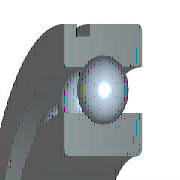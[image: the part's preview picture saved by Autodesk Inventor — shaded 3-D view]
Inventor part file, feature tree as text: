
AUTODESK INVENTOR PART (.ipt)
format: ipt  version: 2015 (Build 190159000, 159)  size: 322,560 bytes
history: native  units: mm (DEFAULTED — no unit token found)
features: sketch x1, other x1, pattern_circular x1
ambient origin geometry x8: Origin, YZ Plane, XZ Plane, XY Plane, X Axis, Y Axis, Z Axis, Center Point
bodies: Solid1 (feature_tree)
feature tree (3):
  sketch  "草图"  dims[d0=7.02mm d17=90.0deg d18=90.0deg d1=1.0mm d2=90.0mm d3=360.0deg d4=0.0mm d5=0.0mm d6=0.0mm d7=25.0mm d8=52.0mm d9=38.5mm d10=48.4mm d11=33.802mm d12=33.802mm d13=33.802mm d14=0.0mm d15=15.0mm d16=15.0mm d19=2.5mm d20=5.0mm d22=7.5mm d23=0.0mm d24=0.0mm]
  other  "轴承体"
  pattern_circular  "IDS_ARRAYBALL[SIMPL:T]"  Angle=90.0deg  [1 undecoded]
note: 1 required parameter value undecoded (feature->parameter linkage not recoverable at this tier; creation-order binding heuristic only, values carry confidence <= 0.55)
